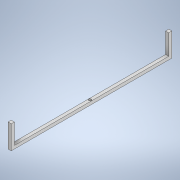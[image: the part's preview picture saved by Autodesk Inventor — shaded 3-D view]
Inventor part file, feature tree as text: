
AUTODESK INVENTOR PART (.ipt)
format: ipt  version: 2020.2 (Build 242310000, 310)  size: 120,832 bytes
history: native  units: mm
features: sketch x2, extrude x2, hole x1
ambient origin geometry x8: Origin, YZ Plane, XZ Plane, XY Plane, X Axis, Y Axis, Z Axis, Center Point
bodies: Body1 (feature_tree)
feature tree (5):
  sketch  "Sketch1"  dims[d0=98.679mm d1=90.0deg]
  extrude  "Extrusion3"  TaperAngle=90.0deg  [1 undecoded]
  extrude  "Extrusion4"  Depth=4.0mm
  hole  "Hole1"  [1 undecoded]
  sketch  "Sketch3"  dims[d2=197.358mm d3=4.0mm d4=4.0mm d5=4.0mm d11=4.0mm d12=0.0mm d13=30.0mm d14=0.0mm d15=2.0mm d16=3.4mm d17=6.0mm d18=6.3mm d19=2.0mm d20=90.0deg d21=8.0mm d22=20.594885mm d6=0.5mm d7=0.872665mm d8=0.5mm d9=0.872665mm]
note: 2 required parameter values undecoded (feature->parameter linkage not recoverable at this tier; creation-order binding heuristic only, values carry confidence <= 0.55)
